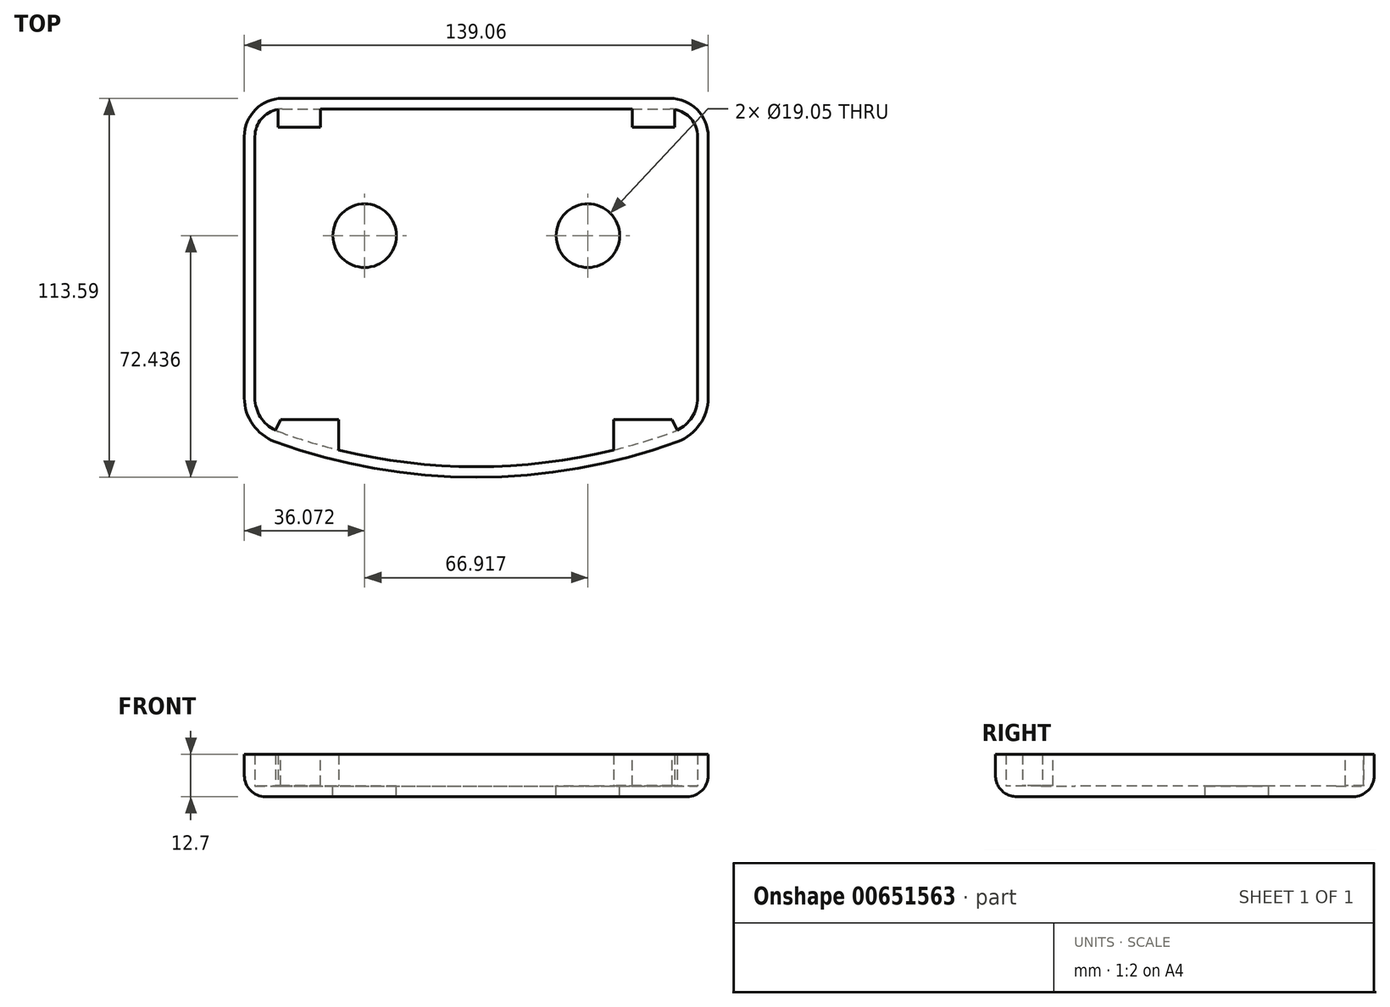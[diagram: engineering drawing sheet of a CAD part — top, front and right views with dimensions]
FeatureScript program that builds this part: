
annotation { "Feature Type Name" : "Feature", "Feature Type Description" : "" }
export const myFeature = defineFeature(function(context is Context, id is Id, definition is map)
    precondition{}
    {
        {
            var Q0;
            Q0=qCreatedBy(makeId("Top.planeOp"),FACE);
            var sketch = newSketch(context, id + "F0", { "sketchPlane" : qUnion([Q0])});
            skLineSegment(sketch, "E0", {"start": v(-58.1, 62.54) * mm, "end": v(58.1, 62.54) * mm});
            skArc(sketch, "E1", {"start": v(-60.37, -40.31) * mm, "mid": v(0, -51.05) * mm, "end": v(60.37, -40.31) * mm});
            skPoint(sketch, "E2", {"position": v(0, -51.05) * mm});
            skLineSegment(sketch, "E3", {"start": v(-69.53, 51.1) * mm, "end": v(-69.53, -27.2) * mm});
            skLineSegment(sketch, "E4.MirrorCS", {"start": v(69.53, 51.1) * mm, "end": v(69.53, -27.2) * mm});
            skPoint(sketch, "E5.orphan", {"position": v(-69.53, -43.52) * mm});
            skPoint(sketch, "E6.orphan", {"position": v(69.53, -43.52) * mm});
            skPoint(sketch, "E7.visualSharp", {"position": v(-69.53, 62.54) * mm});
            skArc(sketch, "E7.filletArc", {"start": v(-58.1, 62.54) * mm, "mid": v(-66.18, 59.19) * mm, "end": v(-69.53, 51.1) * mm});
            skPoint(sketch, "E8.visualSharp", {"position": v(69.53, 62.54) * mm});
            skArc(sketch, "E8.filletArc", {"start": v(69.53, 51.1) * mm, "mid": v(66.18, 59.19) * mm, "end": v(58.1, 62.54) * mm});
            skPoint(sketch, "E9.visualSharp", {"position": v(-69.53, -36.66) * mm});
            skArc(sketch, "E9.filletArc", {"start": v(-69.53, -27.2) * mm, "mid": v(-67.01, -35.2) * mm, "end": v(-60.37, -40.31) * mm});
            skPoint(sketch, "E10.visualSharp", {"position": v(69.53, -36.66) * mm});
            skArc(sketch, "E10.filletArc", {"start": v(60.37, -40.31) * mm, "mid": v(67.01, -35.2) * mm, "end": v(69.53, -27.2) * mm});
            skSolve(sketch);
        }
        {
            var Q0;
            Q0=makeQuery(id+"F0.imprint","IMPRINT",FACE,{"disambiguationData":[TD([[makeQuery(id+"F0.imprint","IMPRINT",EDGE,{"derivedFrom":sQuery(id+"F0.wireOp",EDGE,"E0")}),-1.0]])]});
            extrude(context, id + "F1", {"entities" : qUnion([Q0]), "depth" : 12.7 * mm, "offsetDistance" : 25.4 * mm});
        }
        {
            var Q0;
            Q0=makeQuery(id+"F1.opExtrude","CAP_FACE",FACE,{"disambiguationData":[OSD([sQuery(id+"F0.wireOp",EDGE,"E0"),sQuery(id+"F0.wireOp",EDGE,"E1"),sQuery(id+"F0.wireOp",EDGE,"E3"),sQuery(id+"F0.wireOp",EDGE,"E4.MirrorCS"),sQuery(id+"F0.wireOp",EDGE,"E7.filletArc"),sQuery(id+"F0.wireOp",EDGE,"E8.filletArc"),sQuery(id+"F0.wireOp",EDGE,"E9.filletArc"),sQuery(id+"F0.wireOp",EDGE,"E10.filletArc")])],"isStart":false});
            shell(context, id + "F2", {"entities" : qUnion([Q0]), "thickness" : 3.17 * mm});
        }
        {
            var Q0;
            Q0=makeQuery(id+"F1.opExtrude","CAP_FACE",FACE,{"disambiguationData":[OSD([sQuery(id+"F0.wireOp",EDGE,"E0"),sQuery(id+"F0.wireOp",EDGE,"E1"),sQuery(id+"F0.wireOp",EDGE,"E3"),sQuery(id+"F0.wireOp",EDGE,"E4.MirrorCS"),sQuery(id+"F0.wireOp",EDGE,"E7.filletArc"),sQuery(id+"F0.wireOp",EDGE,"E8.filletArc"),sQuery(id+"F0.wireOp",EDGE,"E9.filletArc"),sQuery(id+"F0.wireOp",EDGE,"E10.filletArc")])],"isStart":true});
            fillet(context, id + "F3", {"entities" : qUnion([Q0]), "radius" : 6.35 * mm, "tangentPropagation" : true, "allowEdgeOverflow" : false});
        }
        {
            var Q0;
            Q0=qCreatedBy(makeId("Top.planeOp"),FACE);
            cPlane(context, id + "F4", {"entities" : qUnion([Q0]), "cplaneType" : CPlaneType.OFFSET, "offset" : 12.7 * mm, "width" : 152.4 * mm, "height" : 152.4 * mm});
        }
        {
            var Q0;
            Q0=qCreatedBy(id+"F4.planeOp",FACE);
            var sketch = newSketch(context, id + "F5", { "sketchPlane" : qUnion([Q0])});
            skLineSegment(sketch, "E11.MirrorCS", {"start": v(46.73, 60.26) * mm, "end": v(46.73, 53.9) * mm});
            skLineSegment(sketch, "E12.MirrorCS", {"start": v(46.73, 60.26) * mm, "end": v(59.43, 60.26) * mm});
            skLineSegment(sketch, "E13.MirrorCS", {"start": v(46.73, 53.9) * mm, "end": v(59.43, 53.9) * mm});
            skLineSegment(sketch, "E14.MirrorCS", {"start": v(59.43, 60.26) * mm, "end": v(59.43, 53.9) * mm});
            skLineSegment(sketch, "E15", {"start": v(-58.7, -33.77) * mm, "end": v(-60.64, -37.91) * mm});
            skLineSegment(sketch, "E16", {"start": v(-60.64, -37.91) * mm, "end": v(-53.9, -40.27) * mm});
            skLineSegment(sketch, "E17.MirrorCS", {"start": v(58.7, -33.77) * mm, "end": v(60.64, -37.91) * mm});
            skLineSegment(sketch, "E18.MirrorCS", {"start": v(60.64, -37.91) * mm, "end": v(53.9, -40.27) * mm});
            skLineSegment(sketch, "E19.MirrorCS", {"start": v(-59.43, 60.26) * mm, "end": v(-59.43, 53.9) * mm});
            skLineSegment(sketch, "E20.MirrorCS", {"start": v(-46.73, 53.9) * mm, "end": v(-59.43, 53.9) * mm});
            skLineSegment(sketch, "E21.MirrorCS", {"start": v(-46.73, 60.26) * mm, "end": v(-46.73, 53.9) * mm});
            skLineSegment(sketch, "E22.MirrorCS", {"start": v(-46.73, 60.26) * mm, "end": v(-59.43, 60.26) * mm});
            skLineSegment(sketch, "E23", {"start": v(-58.7, -33.77) * mm, "end": v(-41.19, -33.77) * mm});
            skLineSegment(sketch, "E24", {"start": v(-41.19, -33.77) * mm, "end": v(-41.19, -43.32) * mm});
            skLineSegment(sketch, "E25", {"start": v(-41.19, -43.32) * mm, "end": v(-53.9, -40.27) * mm});
            skLineSegment(sketch, "E26.MirrorCS", {"start": v(41.19, -33.77) * mm, "end": v(41.19, -43.32) * mm});
            skLineSegment(sketch, "E27.MirrorCS", {"start": v(58.7, -33.77) * mm, "end": v(41.19, -33.77) * mm});
            skLineSegment(sketch, "E28.MirrorCS", {"start": v(41.19, -43.32) * mm, "end": v(53.9, -40.27) * mm});
            skSolve(sketch);
        }
        {
            var Q0;
            Q0=makeQuery(id+"F5.imprint","IMPRINT",FACE,{"disambiguationData":[TD([[makeQuery(id+"F5.imprint","IMPRINT",EDGE,{"derivedFrom":sQuery(id+"F5.wireOp",EDGE,"E19.MirrorCS")}),1.0]])]});
            var Q1;
            Q1=makeQuery(id+"F5.imprint","IMPRINT",FACE,{"disambiguationData":[TD([[makeQuery(id+"F5.imprint","IMPRINT",EDGE,{"derivedFrom":sQuery(id+"F5.wireOp",EDGE,"9519add0-a8e1-4df8-8314-173779524e8a")}),1.0]])]});
            var Q2;
            Q2=makeQuery(id+"F5.imprint","IMPRINT",FACE,{"disambiguationData":[TD([[makeQuery(id+"F5.imprint","IMPRINT",EDGE,{"derivedFrom":sQuery(id+"F5.wireOp",EDGE,"E11.MirrorCS")}),1.0]])]});
            var Q3;
            Q3=makeQuery(id+"F5.imprint","IMPRINT",FACE,{"disambiguationData":[TD([[makeQuery(id+"F5.imprint","IMPRINT",EDGE,{"derivedFrom":sQuery(id+"F5.wireOp",EDGE,"307c7df9-c839-4614-8c11-209d964d54c6.MirrorCS")}),-1.0]])]});
            var Q4;
            Q4=makeQuery(id+"F5.imprint","IMPRINT",FACE,{"disambiguationData":[TD([[makeQuery(id+"F5.imprint","IMPRINT",EDGE,{"derivedFrom":sQuery(id+"F5.wireOp",EDGE,"E15")}),1.0]])]});
            var Q5;
            Q5=makeQuery(id+"F5.imprint","IMPRINT",FACE,{"disambiguationData":[TD([[makeQuery(id+"F5.imprint","IMPRINT",EDGE,{"derivedFrom":sQuery(id+"F5.wireOp",EDGE,"E17.MirrorCS")}),-1.0]])]});
            extrude(context, id + "F6", {"entities" : qUnion([Q0, Q1, Q2, Q3, Q4, Q5]), "operationType" : NewBodyOperationType.ADD, "oppositeDirection" : true, "depth" : 9.4 * mm, "offsetDistance" : 25.4 * mm});
        }
        {
            var Q0;
            Q0=makeQuery(id+"F2.opShell","OFFSET_FACE",FACE,{"disambiguationData":[OSD([sQuery(id+"F0.wireOp",EDGE,"E0"),sQuery(id+"F0.wireOp",EDGE,"E1"),sQuery(id+"F0.wireOp",EDGE,"E3"),sQuery(id+"F0.wireOp",EDGE,"E4.MirrorCS"),sQuery(id+"F0.wireOp",EDGE,"E7.filletArc"),sQuery(id+"F0.wireOp",EDGE,"E8.filletArc"),sQuery(id+"F0.wireOp",EDGE,"E9.filletArc"),sQuery(id+"F0.wireOp",EDGE,"E10.filletArc")])]});
            var sketch = newSketch(context, id + "F7", { "sketchPlane" : qUnion([Q0])});
            skCircle(sketch, "E29", {"center": v(-33.46, 21.39) * mm, "radius": 9.53 * mm});
            skCircle(sketch, "E30", {"center": v(33.46, 21.39) * mm, "radius": 9.53 * mm});
            skSolve(sketch);
        }
        {
            var Q0;
            Q0=makeQuery(id+"F7.imprint","IMPRINT",FACE,{"disambiguationData":[TD([[makeQuery(id+"F7.imprint","IMPRINT",EDGE,{"derivedFrom":sQuery(id+"F7.wireOp",EDGE,"E29")}),1.0]])]});
            var Q1;
            Q1=makeQuery(id+"F7.imprint","IMPRINT",FACE,{"disambiguationData":[TD([[makeQuery(id+"F7.imprint","IMPRINT",EDGE,{"derivedFrom":sQuery(id+"F7.wireOp",EDGE,"E30")}),1.0]])]});
            var Q2;
            Q2=sQuery(id+"F7.wireOp",EDGE,"E29");
            var Q3;
            Q3=sQuery(id+"F7.wireOp",EDGE,"E30");
            extrude(context, id + "F8", {"entities" : qUnion([Q0, Q1]), "operationType" : NewBodyOperationType.REMOVE, "surfaceEntities" : qUnion([Q2, Q3]), "oppositeDirection" : true, "depth" : 25.4 * mm, "offsetDistance" : 25.4 * mm});
        }
    });
